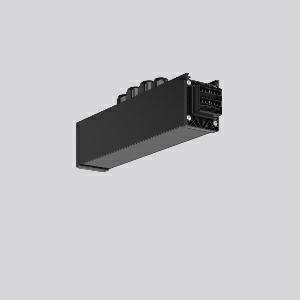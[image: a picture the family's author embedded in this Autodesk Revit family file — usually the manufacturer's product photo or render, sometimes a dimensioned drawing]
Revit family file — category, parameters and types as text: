
# Revit family: linedo_mitteleinspeisung_7pol_982698_003_3_4c1b
name_source: partatom
category: Lighting Fixtures
units: mm (PartAtom-declared; Revit-internal decimal feet)

## family parameters
Cut with Voids When Loaded = No
Host = Face
Light Source = No
Part Type = Normal
Room Calculation Point = No
Round Connector Dimension = Use Diameter
Shared = No

## types (1)
- LINEDO_Mitteleinspeisung_7pol
    Apparent Load = 0 VA
    Default Elevation = 1800 mm
    Description = Series: LINEDO
Middle power feed, 7-pole, connection socket / plug. Housing: extruded aluminium profile, powder-coated. Cover made of plastic, surface like housing. LINEDO plug system, plastic, black. 4 cable glands (2 x M20 and 2 x M25). Cable glands on top. Easy connection for rigid or flexible wires.
Colour: black
Length: 330 mm
Width: 58 mm
Height: 76 mm
Weight: 751 g
    Height = 76 mm
    Lamp = 0 x
    Length = 330 mm
    Luminous efficacy = 0 lm/W
    Manufacturer = RZB
    ModVariant = No
    Model = 982698.003.3
    Mounting Place = Ceiling
    Mounting Type = Surface mounted, Pendant
    Number of Poles = 1
    OnlyDefault = Yes
    Power Factor = 1
    Product Name = LINEDO_Mitteleinspeisung_7pol
    Product group = Surface mounted continuous line luminaire system
    ProductGroupID = 310
    Protection Class = Protection class I
    Protection Degree = IP 54
    RLX_Detail_Level = 1
    RLX_Emergency_Light_Flux = 0 lm
    RLX_Emergency_Type = 0
    RLX_Emergency_Type_DB = No
    RlxData = <blob elided: 23317 chars, md5=e2aba8aa>
    Standby Power = 0 W
    System Light Flux = 0 lm
    System Power = 0 W
    Type Comments = Product without accessories
    Type Image = 982698.003.jpg
    URL = http://relux.com
    VarID = ---
    Voltage = 0 V
    Weight = 0.00 kg
    Width = 58 mm

## geometry (parser evidence)
native form markers: Blend x4, Sweep x10
no freeform markers — native parametric forms only
